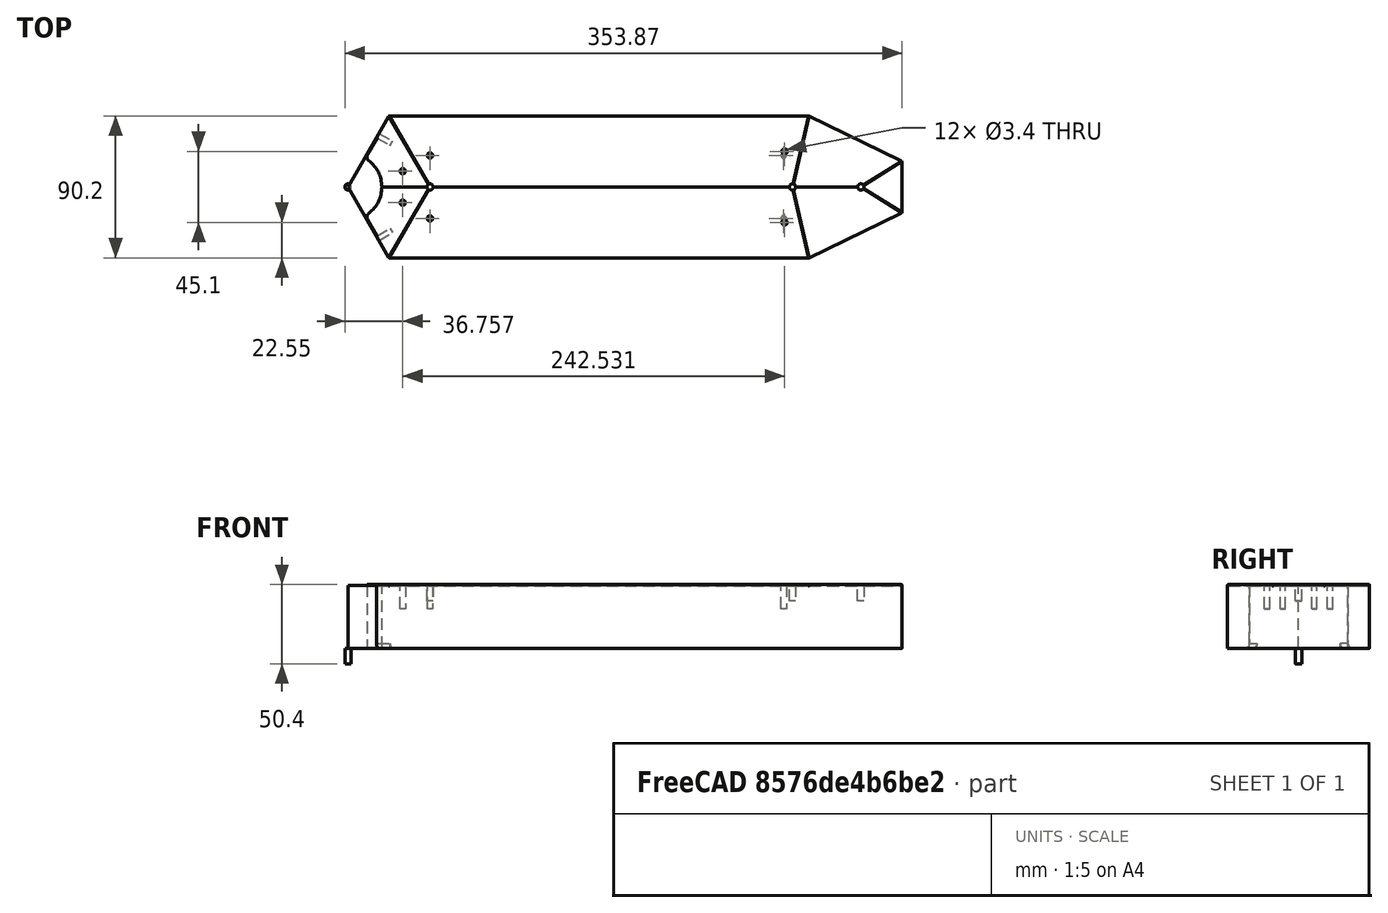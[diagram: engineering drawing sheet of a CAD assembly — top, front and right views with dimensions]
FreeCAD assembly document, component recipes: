
FREECAD ASSEMBLY — COMPONENT RECIPES ("composit_stand3_dropper_fix_cap_outer_model")

This assembly document has 2 components, labeled P0..P1 below (a component is one placed body or linked part). 2 of them carry a construction recipe — the FreeCAD feature program that regenerates the part from scratch, quoted from this document or its linked companion documents; the rest are supplied as boundary geometry only. No exploded tour is included for this assembly.
COMPONENT P0 — recipe-attached ("cap_outer_dropper_fix", modeled in this document).
Construction recipe (the document's own serialized feature program — sketch geometry with constraints, then the solid features built on it; lengths are millimeters unless a unit is written):

FEATURE [PartDesign::SubShapeBinder] Binder001
  BindCopyOnChange = 0
  BindMode = 0
  ClaimChildren = true
  Context = -> Body [Binder001.]
  Fuse = false
  MakeFace = true
  OffsetFill = false
  OffsetIntersection = false
  OffsetJoinType = 0
  OffsetOpenResult = false
  PartialLoad = false
  Relative = false
  Support = -> [Connect]
  _Version = 2
FEATURE [PartDesign::SubShapeBinder] Binder003
  BindCopyOnChange = 0
  BindMode = 0
  ClaimChildren = false
  Context = -> Body [Binder003.]
  Fuse = false
  MakeFace = true
  OffsetFill = false
  OffsetIntersection = false
  OffsetJoinType = 0
  OffsetOpenResult = false
  PartialLoad = false
  Placement = pos=(0,0,39.6) rot=(0,0,1;0rad)
  Relative = true
  Support = -> [Connect001]
  _Version = 2
  expr: .Placement.Base.z = <<BaseBend>>.length
FEATURE [PartDesign::FeaturePython] BaseBend  # WARN: FeaturePython — macro-defined, semantics opaque (R4)
  BendSide = 1
  BendSketch = -> Binder001
  MidPlane = false
  Reverse = false
  Suppressed = false
  length = 39.6
  radius = 0.1
  thickness = 0.3
  expr: length = <<composit_stand3_dropper_fix_cap_outer_main>>#<<Properties>>.height - radius - thickness
FEATURE [PartDesign::FeaturePython] Extend  # WARN: FeaturePython — macro-defined, semantics opaque (R4)
  BaseFeature = -> BaseBend
  Offset = 0.02
  Refine = true
  Suppressed = false
  UseSubtraction = false
  baseObject = -> BaseBend [Face1]
  gap1 = 0
  gap2 = 0
  length = 0
FEATURE [PartDesign::FeaturePython] Bend  # WARN: FeaturePython — macro-defined, semantics opaque (R4)
  AutoMiter = false
  BaseFeature = -> Extend
  BendType = 0
  LengthList = [45.1]
  LengthSpec = 1
  NonperforationMaxLength = 5
  Perforate = false
  PerforationAngle = 0
  PerforationInitialLength = 5
  PerforationMaxLength = 5
  ReliefFactor = 0.7
  Suppressed = false
  UseReliefFactor = false
  angle = 90
  baseObject = -> Extend [Edge4,Edge17,Edge33,Edge107,Edge62,Edge79,Edge95]
  bendAList = [90]
  extend1 = 0
  extend2 = 0
  gap1 = 0
  gap2 = 0
  invert = false
  kfactor = 0.5
  length = 45.1
  maxExtendDist = 5
  minGap = 0.2
  minReliefGap = 1
  miterangle1 = 0
  miterangle2 = 0
  offset = 0
  radius = 0.1
  reliefType = 0
  reliefd = 1
  reliefw = 0.8
  sketchflip = false
  sketchinvert = false
  unfold = false
  expr: radius = BaseBend.radius
FEATURE [PartDesign::Pocket] Pocket
  BaseFeature = -> Bend
  Direction = (0,0,-1)
  Length = 5
  Length2 = 5
  Profile = -> Binder003
  Refine = true
  Reversed = true
  Suppressed = false
  Type = 0
FEATURE [PartDesign::CoordinateSystem] Local_CS
  AttacherType = Attacher::AttachEngine3D
  AttachmentSupport = -> [XY_Plane]
  MapMode = 5
FEATURE [PartDesign::Boolean] Boolean
  BaseFeature = -> Pocket
  Group = -> [Fusion]
  Suppressed = false
  Type = 1
  UsePlacement = true
FEATURE [PartDesign::Body] Body  label="cap_outer_dropper_fix"
  AllowCompound = false
  Group = -> [Binder001,Binder003,BaseBend,Extend,Bend,Pocket,Boolean,Local_CS]
  Origin = -> Origin
  Tip = -> Boolean
COMPONENT P1 — recipe-attached ("hole_3.4mm_rev", a linked part whose construction recipe lives in a companion FreeCAD document of the same project; that document's serialized recipe follows).
Construction recipe (the companion document, serialized — sketch geometry with constraints, then the solid features built on it; lengths are millimeters unless a unit is written):

FCSTD DOCUMENT  (FreeCAD 1.1R38827 (Git))
Label: composit_stand3_main
License: All rights reserved
LicenseURL: http://en.wikipedia.org/wiki/All_rights_reserved
objects: Part::Cylinder×2, Sketcher::SketchObject×1, Part::FeaturePython×1
note: 5 computed .brp shape members not serialized (recipe doc carries the construction recipe); baked Part::Feature solids carry a one-line shape summary decoded from their .brp

FEATURE [Sketcher::SketchObject] Sketch  label="main_sketch"
  ArcFitTolerance = 0
  FullyConstrained = true
  MakeInternals = false
  sketch-geometry (4):
    g0: LineSegment [constr] StartX=0 StartY=0 StartZ=0 EndX=8.37158 EndY=14.5 EndZ=0
    g1: LineSegment StartX=8.37158 StartY=14.5 StartZ=0 EndX=351.872 EndY=14.5 EndZ=0
    g2: LineSegment StartX=351.872 StartY=14.5 StartZ=0 EndX=351.872 EndY=0 EndZ=0
    g3: GeomPoint [constr] X=351.872 Y=-14.5 Z=0
  constraints (13):
    c: Coincident(g-1,g0)
    c: Horizontal(g1)
    c: Coincident(g1,g2)
    c: PointOnObject(g2,g-1)
    c: Vertical(g2)
    c: Angle(g0) = 1.0472
    c: DistanceX(g0,g1) = 343.5  'face_width'
    c: DistanceY(g3,g1) = 29  'end_width'
    c: Symmetric(g3,g1,g2)
    c: DistanceX(g0) = 8.37158  'x_face_offset'
    c: Coincident(g1,g0)
    c: Distance(g0) = 16.7432  'corner_distance'
    c: DistanceY(g0,g0) = 14.5
FEATURE [Part::FeaturePython] LinearArray  label="modules_placement_x"  # WARN: FeaturePython — macro-defined, semantics opaque (R4)
  Alignment = 0
  CellStart = A1
  Count = 2
  Dir = (1,0,0)
  DirIsDriven = true
  DistributionLaw = 0
  DrivenProperty = 1
  EndInclusive = true
  ExposePlacement = false
  GeneratorMode = 0
  MarkerShape = 1
  MarkerSize = 0
  NumElements = 2
  OrientMode = 1
  Placement = pos=(8.37158,14.5,0) rot=(0,0,1;0rad)
  Point = (0,0,0)
  PointIsDriven = true
  Reverse = false
  SpanEnd = 248
  SpanStart = 98
  Step = 150
  Type = lattice2LinearArray.LinearArray
  VSGVersion = 1
  Values = 98.0 | 248.0
  ValuesSource = 2
  isLattice = 1
  expr: .Placement.Base.x = <<main_sketch>>.Constraints.end_width / 2 / tan(60)
  expr: .Placement.Base.y = <<main_sketch>>.Constraints.end_width / 2
FEATURE [Part::Cylinder] Cylinder  label="hole_3.4mm"
  Angle = 360
  AttacherType = Attacher::AttachEngine3D
  FirstAngle = 0
  Height = 15
  Radius = 1.7
  SecondAngle = 0
FEATURE [Part::Cylinder] Cylinder001  label="hole_3.4mm_rev"
  Angle = 360
  AttacherType = Attacher::AttachEngine3D
  FirstAngle = 0
  Height = 15
  Placement = pos=(0,0,0) rot=(1,0,0;3.14159rad)
  Radius = 1.7
  SecondAngle = 0
PROVENANCE & LICENSES
A FreeCAD (.FCStd) document from a public repository crawl; recipes are the document's own serialized feature recipes (and, for linked parts, companion documents' recipes).
License: as declared in the source repository (recorded in the dataset sidecar).
